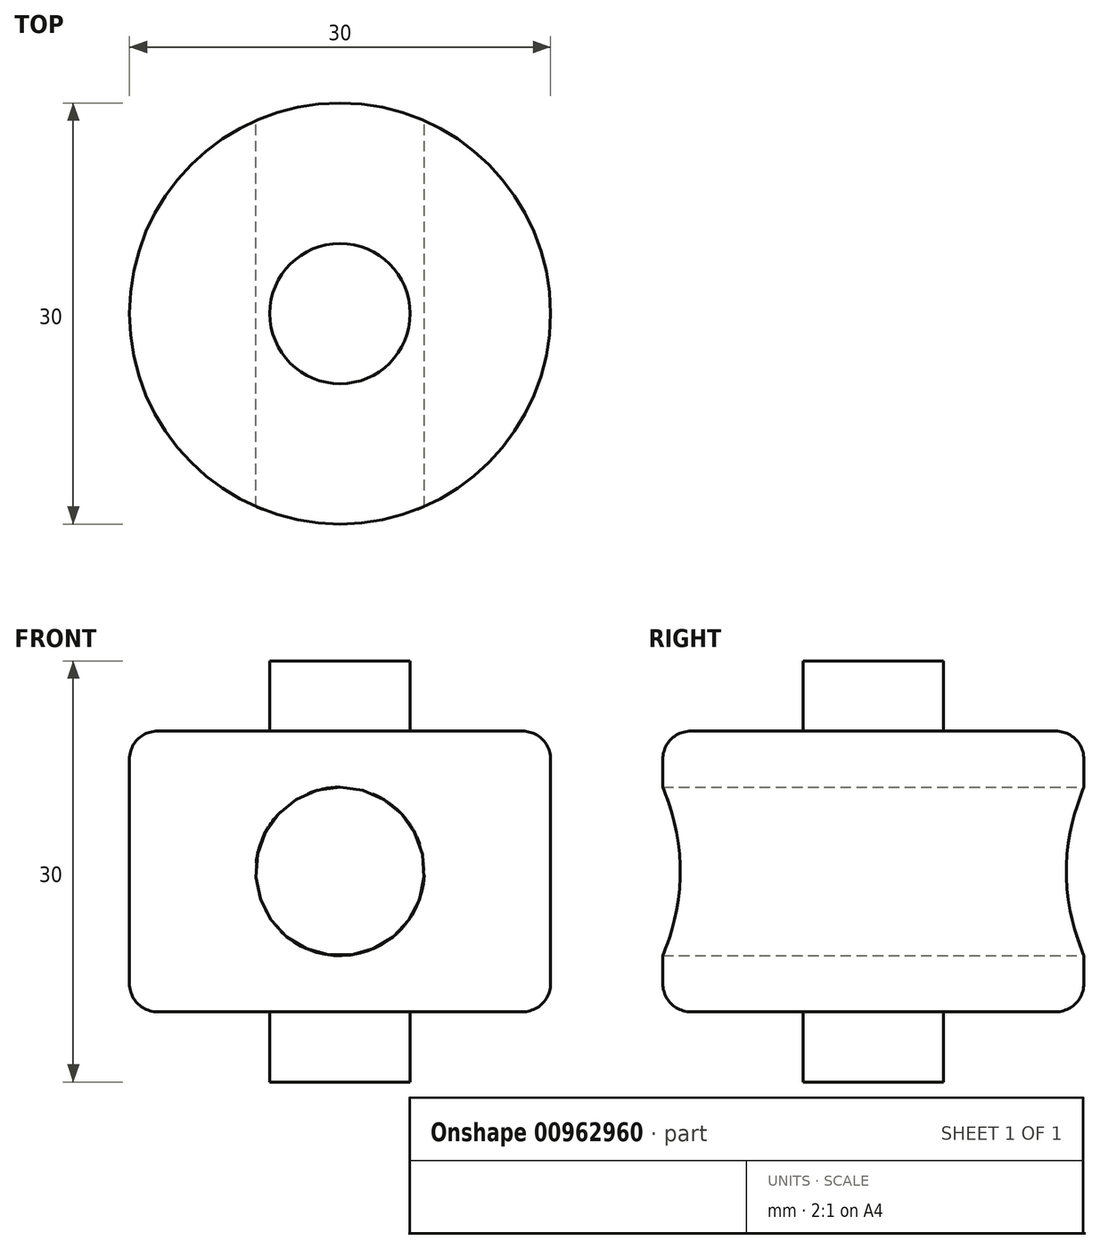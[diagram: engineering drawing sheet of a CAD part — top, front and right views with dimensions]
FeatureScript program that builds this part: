
annotation { "Feature Type Name" : "Feature", "Feature Type Description" : "" }
export const myFeature = defineFeature(function(context is Context, id is Id, definition is map)
    precondition{}
    {
        {
            var Q0;
            Q0=qCreatedBy(makeId("Top.planeOp"),FACE);
            var sketch = newSketch(context, id + "F0", { "sketchPlane" : qUnion([Q0])});
            skCircle(sketch, "E0", {"center": v(0, 0) * mm, "radius": 15 * mm});
            skSolve(sketch);
        }
        {
            var Q0;
            Q0 = qSketchRegion(id + "F0", true);
            extrude(context, id + "F1", {"entities" : qUnion([Q0]), "depth" : 20 * mm, "offsetDistance" : 25 * mm, "symmetric" : true});
        }
        {
            var Q0;
            Q0=makeQuery(id+"F1.opExtrude","CAP_EDGE",EDGE,{"disambiguationData":[OSD([sQuery(id+"F0.wireOp",EDGE,"E0")])],"isStart":false});
            var Q1;
            Q1=makeQuery(id+"F1.opExtrude","CAP_EDGE",EDGE,{"disambiguationData":[OSD([sQuery(id+"F0.wireOp",EDGE,"E0")])],"isStart":true});
            fillet(context, id + "F2", {"entities" : qUnion([Q0, Q1]), "radius" : 2 * mm, "tangentPropagation" : true, "allowEdgeOverflow" : false});
        }
        {
            var Q0;
            Q0=makeQuery(id+"F1.opExtrude","CAP_FACE",FACE,{"disambiguationData":[OSD([sQuery(id+"F0.wireOp",EDGE,"E0")])],"isStart":false});
            var sketch = newSketch(context, id + "F3", { "sketchPlane" : qUnion([Q0])});
            skCircle(sketch, "E1", {"center": v(0, 0) * mm, "radius": 5 * mm});
            skSolve(sketch);
        }
        {
            var Q0;
            Q0 = qSketchRegion(id + "F3", true);
            extrude(context, id + "F4", {"entities" : qUnion([Q0]), "operationType" : NewBodyOperationType.ADD, "depth" : 5 * mm, "offsetDistance" : 25 * mm});
        }
        {
            var Q0;
            Q0=makeQuery(id+"F1.opExtrude","CAP_FACE",FACE,{"disambiguationData":[OSD([sQuery(id+"F0.wireOp",EDGE,"E0")])],"isStart":true});
            var sketch = newSketch(context, id + "F5", { "sketchPlane" : qUnion([Q0])});
            skCircle(sketch, "E2", {"center": v(0, 0) * mm, "radius": 5 * mm});
            skSolve(sketch);
        }
        {
            var Q0;
            Q0 = qSketchRegion(id + "F5", true);
            extrude(context, id + "F6", {"entities" : qUnion([Q0]), "operationType" : NewBodyOperationType.ADD, "depth" : 5 * mm, "offsetDistance" : 25 * mm});
        }
        {
            var Q0;
            Q0=qCreatedBy(makeId("Front.planeOp"),FACE);
            var sketch = newSketch(context, id + "F7", { "sketchPlane" : qUnion([Q0])});
            skCircle(sketch, "E3", {"center": v(0, 0) * mm, "radius": 6 * mm});
            skSolve(sketch);
        }
        {
            var Q0;
            Q0 = qSketchRegion(id + "F7", true);
            extrude(context, id + "F8", {"entities" : qUnion([Q0]), "operationType" : NewBodyOperationType.REMOVE, "endBound" : BoundingType.THROUGH_ALL, "depth" : 25 * mm, "offsetDistance" : 25 * mm, "hasSecondDirection" : true, "secondDirectionBound" : BoundingType.THROUGH_ALL, "secondDirectionOppositeDirection" : true, "secondDirectionDepth" : 25 * mm});
        }
    });
